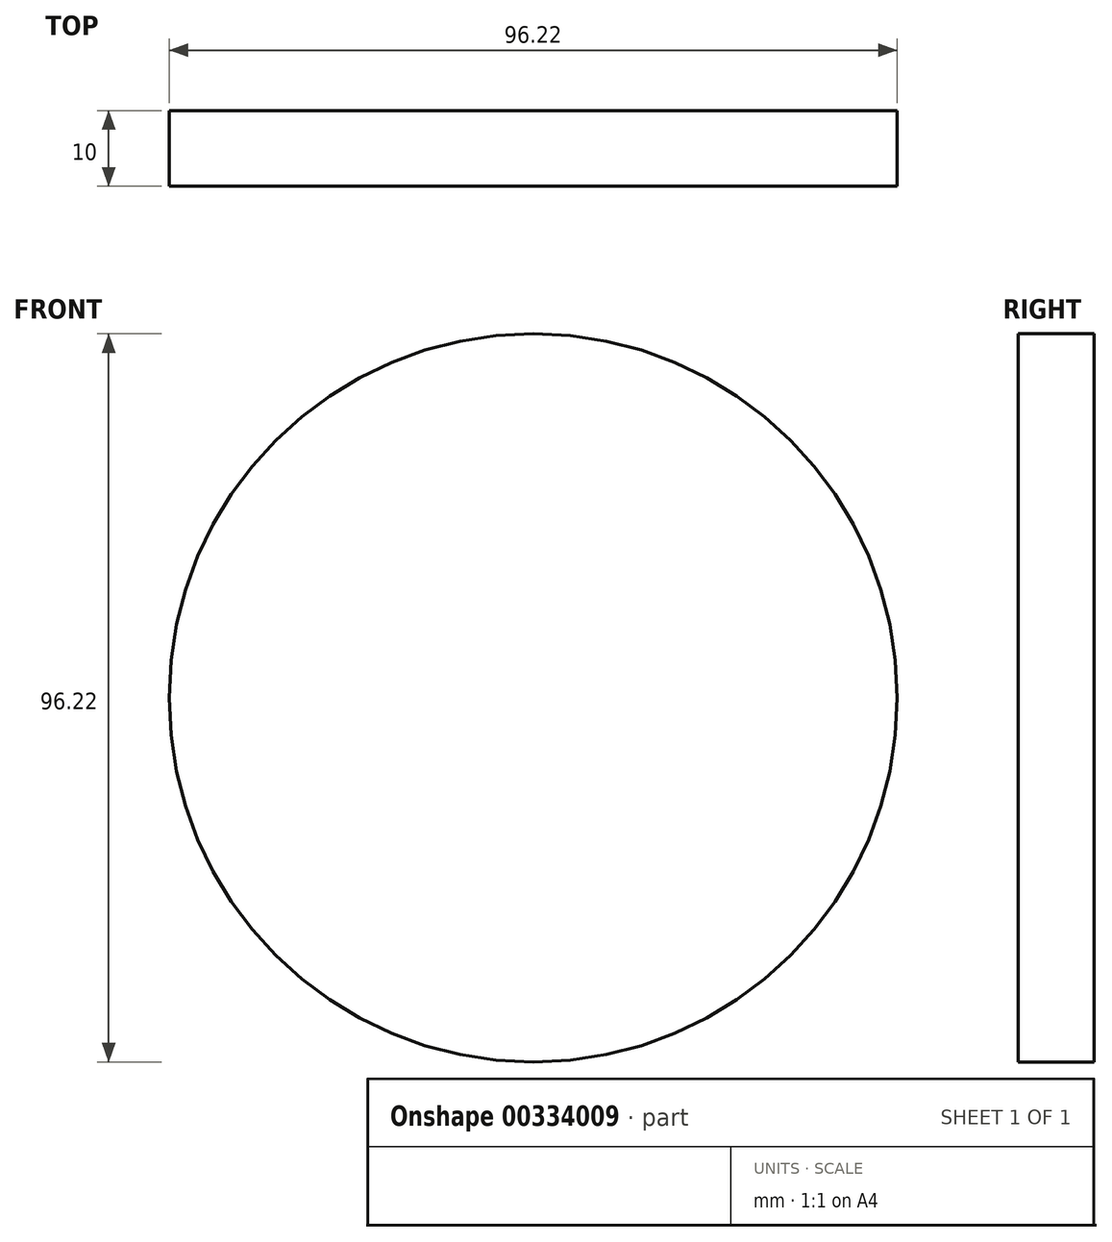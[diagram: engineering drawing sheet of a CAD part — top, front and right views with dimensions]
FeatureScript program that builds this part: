
annotation { "Feature Type Name" : "Feature", "Feature Type Description" : "" }
export const myFeature = defineFeature(function(context is Context, id is Id, definition is map)
    precondition{}
    {
        {
            var Q0;
            Q0=qCreatedBy(makeId("Front.planeOp"),FACE);
            var sketch = newSketch(context, id + "F0", { "sketchPlane" : qUnion([Q0])});
            skCircle(sketch, "E0", {"center": v(0, 0) * mm, "radius": 48.11 * mm});
            skSolve(sketch);
        }
        {
            var Q0;
            Q0=makeQuery(id+"F0.imprint","IMPRINT",FACE,{"disambiguationData":[TD([[makeQuery(id+"F0.imprint","IMPRINT",EDGE,{"derivedFrom":sQuery(id+"F0.wireOp",EDGE,"E0")}),1.0]])]});
            extrude(context, id + "F1", {"entities" : qUnion([Q0]), "depth" : 10 * mm});
        }
    });
